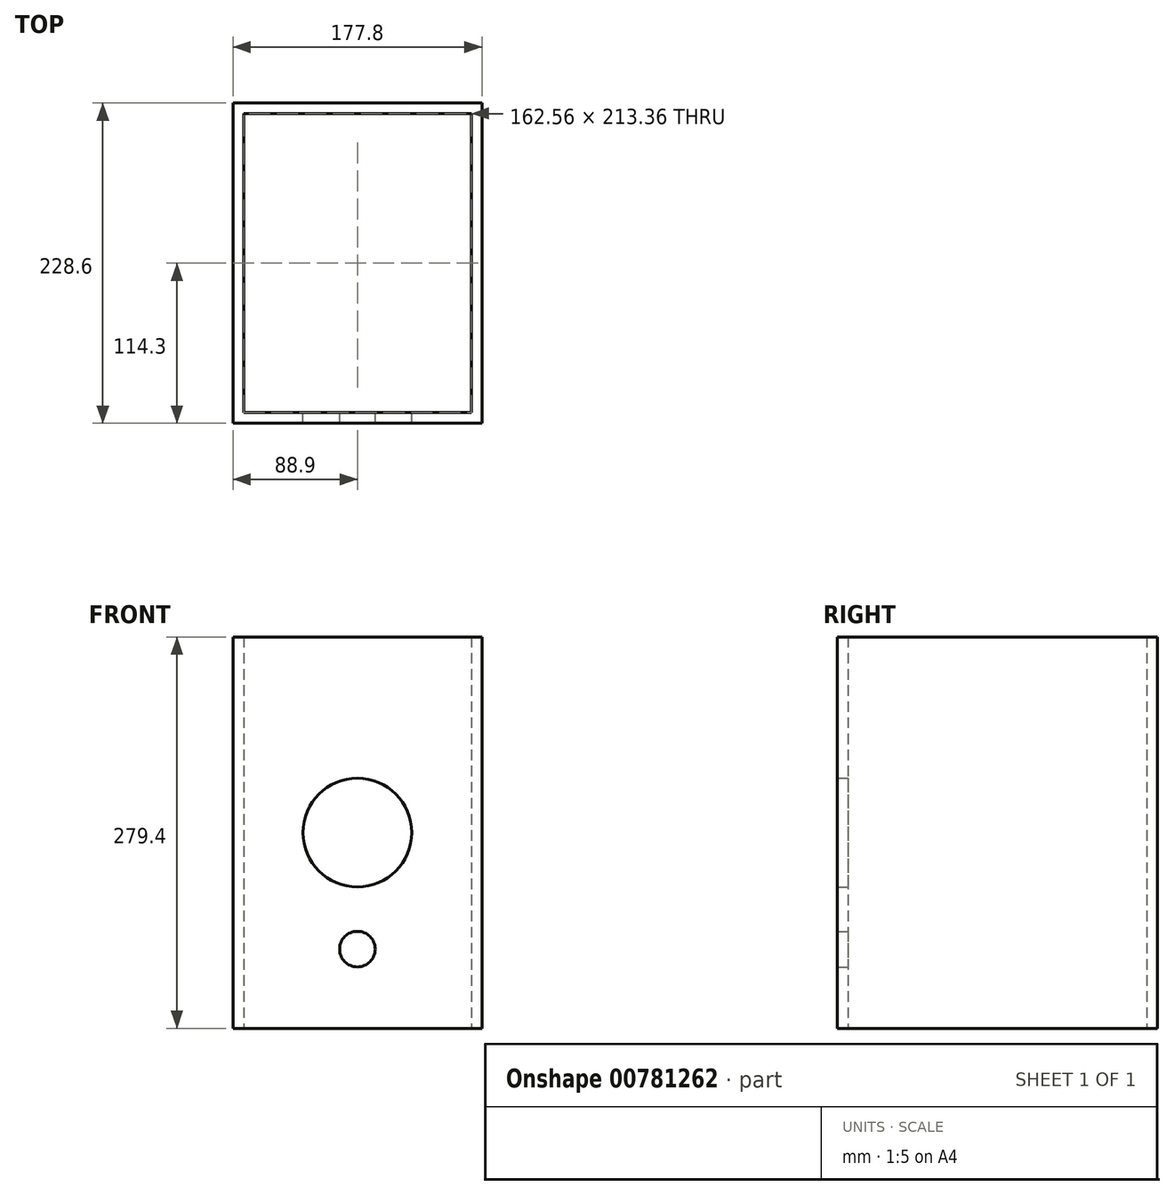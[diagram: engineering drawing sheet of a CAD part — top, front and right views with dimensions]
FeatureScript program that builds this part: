
annotation { "Feature Type Name" : "Feature", "Feature Type Description" : "" }
export const myFeature = defineFeature(function(context is Context, id is Id, definition is map)
    precondition{}
    {
        {
            var Q0;
            Q0=qCreatedBy(makeId("Top.planeOp"),FACE);
            var sketch = newSketch(context, id + "F0", { "sketchPlane" : qUnion([Q0])});
            skLineSegment(sketch, "E0.bottom", {"start": v(-88.9, 114.3) * mm, "end": v(88.9, 114.3) * mm});
            skLineSegment(sketch, "E0.top", {"start": v(-88.9, -114.3) * mm, "end": v(88.9, -114.3) * mm});
            skLineSegment(sketch, "E0.left", {"start": v(-88.9, 114.3) * mm, "end": v(-88.9, -114.3) * mm});
            skLineSegment(sketch, "E0.right", {"start": v(88.9, 114.3) * mm, "end": v(88.9, -114.3) * mm});
            skPoint(sketch, "E0.middle", {"position": v(0, 0) * mm});
            skLineSegment(sketch, "E1.0", {"start": v(-81.28, 106.68) * mm, "end": v(81.28, 106.68) * mm});
            skLineSegment(sketch, "E1.1", {"start": v(-81.28, 106.68) * mm, "end": v(-81.28, -106.68) * mm});
            skLineSegment(sketch, "E1.2", {"start": v(-81.28, -106.68) * mm, "end": v(81.28, -106.68) * mm});
            skLineSegment(sketch, "E1.3", {"start": v(81.28, 106.68) * mm, "end": v(81.28, -106.68) * mm});
            skSolve(sketch);
        }
        {
            var Q0;
            Q0=qSketchRegion(id+"F0",true);
            extrude(context, id + "F1", {"entities" : qUnion([Q0]), "endBound" : BoundingType.SYMMETRIC, "depth" : 279.4 * mm, "offsetDistance" : 25.4 * mm});
        }
        {
            var Q0;
            Q0=qCreatedBy(makeId("Front.planeOp"),FACE);
            var sketch = newSketch(context, id + "F2", { "sketchPlane" : qUnion([Q0])});
            skCircle(sketch, "E2", {"center": v(0, -83.16) * mm, "radius": 12.7 * mm});
            skCircle(sketch, "E3", {"center": v(0, 0) * mm, "radius": 38.83 * mm});
            skSolve(sketch);
        }
        {
            var Q0;
            Q0=qSketchRegion(id+"F2",true);
            extrude(context, id + "F3", {"entities" : qUnion([Q0]), "operationType" : NewBodyOperationType.REMOVE, "depth" : 254 * mm, "offsetDistance" : 25.4 * mm});
        }
    });
